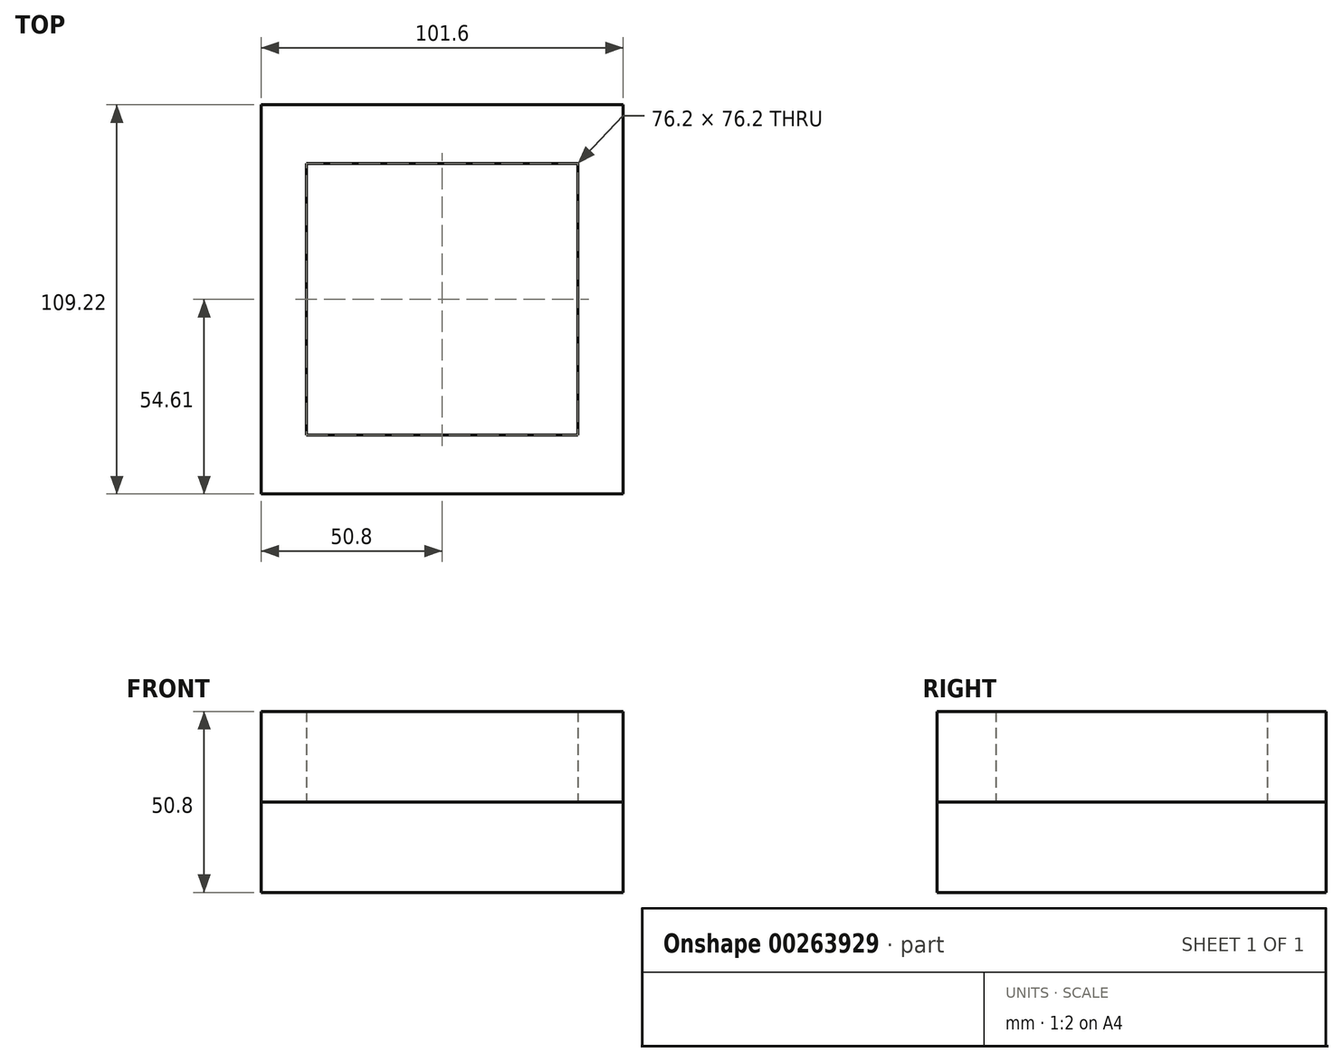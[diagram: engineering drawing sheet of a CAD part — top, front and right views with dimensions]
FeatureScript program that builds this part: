
annotation { "Feature Type Name" : "Feature", "Feature Type Description" : "" }
export const myFeature = defineFeature(function(context is Context, id is Id, definition is map)
    precondition{}
    {
        {
            var Q0;
            Q0=qCreatedBy(makeId("Top.planeOp"),FACE);
            var sketch = newSketch(context, id + "F0", { "sketchPlane" : qUnion([Q0])});
            skLineSegment(sketch, "E0.bottom", {"start": v(50.8, -54.6) * mm, "end": v(-50.8, -54.61) * mm});
            skLineSegment(sketch, "E0.top", {"start": v(50.8, 54.61) * mm, "end": v(-50.8, 54.61) * mm});
            skLineSegment(sketch, "E0.left", {"start": v(50.8, -54.6) * mm, "end": v(50.8, 54.61) * mm});
            skLineSegment(sketch, "E0.right", {"start": v(-50.8, -54.61) * mm, "end": v(-50.8, 54.61) * mm});
            skPoint(sketch, "E0.middle", {"position": v(0, 0) * mm});
            skLineSegment(sketch, "E1.bottom", {"start": v(38.1, -38.1) * mm, "end": v(-38.1, -38.1) * mm});
            skLineSegment(sketch, "E1.top", {"start": v(38.1, 38.1) * mm, "end": v(-38.1, 38.1) * mm});
            skLineSegment(sketch, "E1.left", {"start": v(38.1, -38.1) * mm, "end": v(38.1, 38.1) * mm});
            skLineSegment(sketch, "E1.right", {"start": v(-38.1, -38.1) * mm, "end": v(-38.1, 38.1) * mm});
            skSolve(sketch);
        }
        {
            var Q0;
            Q0 = qSketchRegion(id + "F0", true);
            extrude(context, id + "F1", {"entities" : qUnion([Q0]), "depth" : 25.4 * mm});
        }
        {
            var Q0;
            Q0=makeQuery(id+"F0.imprint","IMPRINT",FACE,{"disambiguationData":[TD([[makeQuery(id+"F0.imprint","IMPRINT",EDGE,{"derivedFrom":sQuery(id+"F0.wireOp",EDGE,"E1.bottom")}),-1.0]])]});
            var Q1;
            Q1=makeQuery(id+"F0.imprint","IMPRINT",FACE,{"disambiguationData":[TD([[makeQuery(id+"F0.imprint","IMPRINT",EDGE,{"derivedFrom":sQuery(id+"F0.wireOp",EDGE,"E0.bottom")}),-1.0]])]});
            extrude(context, id + "F2", {"entities" : qUnion([Q0, Q1]), "oppositeDirection" : true, "depth" : 25.4 * mm});
        }
    });
